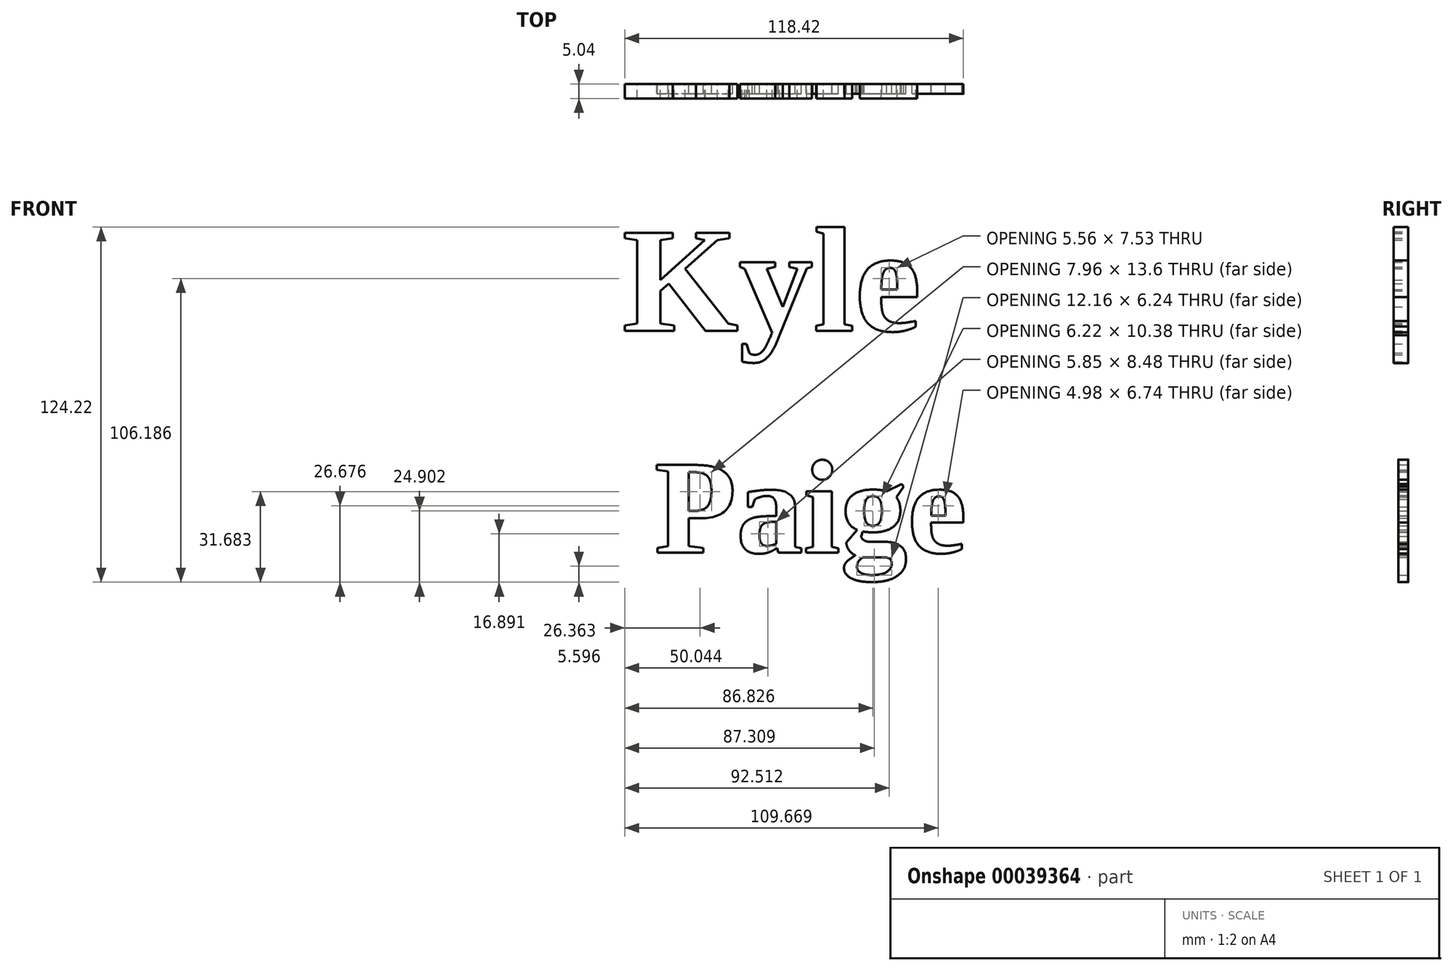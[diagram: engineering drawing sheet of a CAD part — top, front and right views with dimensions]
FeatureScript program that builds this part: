
annotation { "Feature Type Name" : "Feature", "Feature Type Description" : "" }
export const myFeature = defineFeature(function(context is Context, id is Id, definition is map)
    precondition{}
    {
        {
            var Q0;
            Q0=qCreatedBy(makeId("Front.planeOp"),FACE);
            var sketch = newSketch(context, id + "F0", { "sketchPlane" : qUnion([Q0])});
            skText(sketch, "E0", { "text": "Kyle", "fontName": "Tinos-Bold.ttf"});
            const initialGuessF0  = {"E0": [-0.05057, 0.01097, 1, 0, 0.03764]};
            skSetInitialGuess(sketch, initialGuessF0);
            skSolve(sketch);
        }
        {
            var Q0;
            Q0 = qSketchRegion(id + "F0", true);
            extrude(context, id + "F1", {"entities" : qUnion([Q0]), "depth" : 5.04 * mm});
        }
        {
            var Q0;
            Q0=makeQuery(id+"F1.opExtrude","SWEPT_BODY",BODY,{"disambiguationData":[OSD([sQuery(id+"F0.wireOp",EDGE,"E0.sketch_text.stroke-0"),sQuery(id+"F0.wireOp",EDGE,"E0.sketch_text.stroke-1"),sQuery(id+"F0.wireOp",EDGE,"E0.sketch_text.stroke-2"),sQuery(id+"F0.wireOp",EDGE,"E0.sketch_text.stroke-3"),sQuery(id+"F0.wireOp",EDGE,"E0.sketch_text.stroke-4"),sQuery(id+"F0.wireOp",EDGE,"E0.sketch_text.stroke-5"),sQuery(id+"F0.wireOp",EDGE,"E0.sketch_text.stroke-6"),sQuery(id+"F0.wireOp",EDGE,"E0.sketch_text.stroke-7"),sQuery(id+"F0.wireOp",EDGE,"E0.sketch_text.stroke-8"),sQuery(id+"F0.wireOp",EDGE,"E0.sketch_text.stroke-9"),sQuery(id+"F0.wireOp",EDGE,"E0.sketch_text.stroke-10"),sQuery(id+"F0.wireOp",EDGE,"E0.sketch_text.stroke-11"),sQuery(id+"F0.wireOp",EDGE,"E0.sketch_text.stroke-12"),sQuery(id+"F0.wireOp",EDGE,"E0.sketch_text.stroke-13"),sQuery(id+"F0.wireOp",EDGE,"E0.sketch_text.stroke-14"),sQuery(id+"F0.wireOp",EDGE,"E0.sketch_text.stroke-15"),sQuery(id+"F0.wireOp",EDGE,"E0.sketch_text.stroke-16"),sQuery(id+"F0.wireOp",EDGE,"E0.sketch_text.stroke-17"),sQuery(id+"F0.wireOp",EDGE,"E0.sketch_text.stroke-18"),sQuery(id+"F0.wireOp",EDGE,"E0.sketch_text.stroke-19"),sQuery(id+"F0.wireOp",EDGE,"E0.sketch_text.stroke-20"),sQuery(id+"F0.wireOp",EDGE,"E0.sketch_text.stroke-21"),sQuery(id+"F0.wireOp",EDGE,"E0.sketch_text.stroke-22"),sQuery(id+"F0.wireOp",EDGE,"E0.sketch_text.stroke-23"),sQuery(id+"F0.wireOp",EDGE,"E0.sketch_text.stroke-24"),sQuery(id+"F0.wireOp",EDGE,"E0.sketch_text.stroke-25")])]});
            var Q1;
            Q1=makeQuery(id+"F1.opExtrude","SWEPT_BODY",BODY,{"disambiguationData":[OSD([sQuery(id+"F0.wireOp",EDGE,"E0.sketch_text.stroke-26"),sQuery(id+"F0.wireOp",EDGE,"E0.sketch_text.stroke-27"),sQuery(id+"F0.wireOp",EDGE,"E0.sketch_text.stroke-28"),sQuery(id+"F0.wireOp",EDGE,"E0.sketch_text.stroke-29"),sQuery(id+"F0.wireOp",EDGE,"E0.sketch_text.stroke-30"),sQuery(id+"F0.wireOp",EDGE,"E0.sketch_text.stroke-31"),sQuery(id+"F0.wireOp",EDGE,"E0.sketch_text.stroke-32"),sQuery(id+"F0.wireOp",EDGE,"E0.sketch_text.stroke-33"),sQuery(id+"F0.wireOp",EDGE,"E0.sketch_text.stroke-34"),sQuery(id+"F0.wireOp",EDGE,"E0.sketch_text.stroke-35"),sQuery(id+"F0.wireOp",EDGE,"E0.sketch_text.stroke-36"),sQuery(id+"F0.wireOp",EDGE,"E0.sketch_text.stroke-37"),sQuery(id+"F0.wireOp",EDGE,"E0.sketch_text.stroke-38"),sQuery(id+"F0.wireOp",EDGE,"E0.sketch_text.stroke-39"),sQuery(id+"F0.wireOp",EDGE,"E0.sketch_text.stroke-40"),sQuery(id+"F0.wireOp",EDGE,"E0.sketch_text.stroke-41"),sQuery(id+"F0.wireOp",EDGE,"E0.sketch_text.stroke-42"),sQuery(id+"F0.wireOp",EDGE,"E0.sketch_text.stroke-43"),sQuery(id+"F0.wireOp",EDGE,"E0.sketch_text.stroke-44"),sQuery(id+"F0.wireOp",EDGE,"E0.sketch_text.stroke-45"),sQuery(id+"F0.wireOp",EDGE,"E0.sketch_text.stroke-46"),sQuery(id+"F0.wireOp",EDGE,"E0.sketch_text.stroke-47"),sQuery(id+"F0.wireOp",EDGE,"E0.sketch_text.stroke-48"),sQuery(id+"F0.wireOp",EDGE,"E0.sketch_text.stroke-49"),sQuery(id+"F0.wireOp",EDGE,"E0.sketch_text.stroke-50"),sQuery(id+"F0.wireOp",EDGE,"E0.sketch_text.stroke-51")])]});
            var Q2;
            Q2=makeQuery(id+"F1.opExtrude","SWEPT_BODY",BODY,{"disambiguationData":[OSD([sQuery(id+"F0.wireOp",EDGE,"E0.sketch_text.stroke-52"),sQuery(id+"F0.wireOp",EDGE,"E0.sketch_text.stroke-53"),sQuery(id+"F0.wireOp",EDGE,"E0.sketch_text.stroke-54"),sQuery(id+"F0.wireOp",EDGE,"E0.sketch_text.stroke-55"),sQuery(id+"F0.wireOp",EDGE,"E0.sketch_text.stroke-56"),sQuery(id+"F0.wireOp",EDGE,"E0.sketch_text.stroke-57"),sQuery(id+"F0.wireOp",EDGE,"E0.sketch_text.stroke-58"),sQuery(id+"F0.wireOp",EDGE,"E0.sketch_text.stroke-59"),sQuery(id+"F0.wireOp",EDGE,"E0.sketch_text.stroke-60"),sQuery(id+"F0.wireOp",EDGE,"E0.sketch_text.stroke-61")])]});
            var Q3;
            Q3=makeQuery(id+"F1.opExtrude","SWEPT_BODY",BODY,{"disambiguationData":[OSD([sQuery(id+"F0.wireOp",EDGE,"E0.sketch_text.stroke-62"),sQuery(id+"F0.wireOp",EDGE,"E0.sketch_text.stroke-63"),sQuery(id+"F0.wireOp",EDGE,"E0.sketch_text.stroke-64"),sQuery(id+"F0.wireOp",EDGE,"E0.sketch_text.stroke-65"),sQuery(id+"F0.wireOp",EDGE,"E0.sketch_text.stroke-66"),sQuery(id+"F0.wireOp",EDGE,"E0.sketch_text.stroke-67"),sQuery(id+"F0.wireOp",EDGE,"E0.sketch_text.stroke-68"),sQuery(id+"F0.wireOp",EDGE,"E0.sketch_text.stroke-69"),sQuery(id+"F0.wireOp",EDGE,"E0.sketch_text.stroke-70"),sQuery(id+"F0.wireOp",EDGE,"E0.sketch_text.stroke-71"),sQuery(id+"F0.wireOp",EDGE,"E0.sketch_text.stroke-72"),sQuery(id+"F0.wireOp",EDGE,"E0.sketch_text.stroke-73"),sQuery(id+"F0.wireOp",EDGE,"E0.sketch_text.stroke-74"),sQuery(id+"F0.wireOp",EDGE,"E0.sketch_text.stroke-75"),sQuery(id+"F0.wireOp",EDGE,"E0.sketch_text.stroke-76"),sQuery(id+"F0.wireOp",EDGE,"E0.sketch_text.stroke-77"),sQuery(id+"F0.wireOp",EDGE,"E0.sketch_text.stroke-78"),sQuery(id+"F0.wireOp",EDGE,"E0.sketch_text.stroke-79"),sQuery(id+"F0.wireOp",EDGE,"E0.sketch_text.stroke-80"),sQuery(id+"F0.wireOp",EDGE,"E0.sketch_text.stroke-81"),sQuery(id+"F0.wireOp",EDGE,"E0.sketch_text.stroke-82"),sQuery(id+"F0.wireOp",EDGE,"E0.sketch_text.stroke-83")])]});
            var Q4;
            Q4=makeQuery(id+"F1.opExtrude","CAP_VERTEX",VERTEX,{"disambiguationData":[OSD([sQuery(id+"F0.wireOp",EDGE,"E0.sketch_text.stroke-17"),sQuery(id+"F0.wireOp",EDGE,"E0.sketch_text.stroke-18")])],"isStart":false});
            transform(context, id + "F2", {"entities" : qUnion([Q0, Q1, Q2, Q3]), "transformType" : TransformType.SCALE_UNIFORMLY, "scale" : .5, "makeCopy" : false, "scalePoint" : qUnion([Q4])});
        }
        {
            var Q0;
            Q0=qCreatedBy(makeId("Front.planeOp"),FACE);
            var sketch = newSketch(context, id + "F3", { "sketchPlane" : qUnion([Q0])});
            skText(sketch, "E1", { "text": "Paige", "fontName": "Tinos-Bold.ttf"});
            const initialGuessF3  = {"E1": [-0.03925, -0.05045, 1, 0, 0.03371]};
            skSetInitialGuess(sketch, initialGuessF3);
            skSolve(sketch);
        }
        {
            var Q0;
            Q0=makeQuery(id+"F3.imprint","IMPRINT",FACE,{"disambiguationData":[TD([[makeQuery(id+"F3.imprint","IMPRINT",EDGE,{"derivedFrom":sQuery(id+"F3.wireOp",EDGE,"E1.sketch_text.stroke-0")}),-1.0]])]});
            var Q1;
            Q1=makeQuery(id+"F3.imprint","IMPRINT",FACE,{"disambiguationData":[TD([[makeQuery(id+"F3.imprint","IMPRINT",EDGE,{"derivedFrom":sQuery(id+"F3.wireOp",EDGE,"E1.sketch_text.stroke-21")}),-1.0]])]});
            var Q2;
            Q2=makeQuery(id+"F3.imprint","IMPRINT",FACE,{"disambiguationData":[TD([[makeQuery(id+"F3.imprint","IMPRINT",EDGE,{"derivedFrom":sQuery(id+"F3.wireOp",EDGE,"E1.sketch_text.stroke-49")}),-1.0]])]});
            var Q3;
            Q3=makeQuery(id+"F3.imprint","IMPRINT",FACE,{"disambiguationData":[TD([[makeQuery(id+"F3.imprint","IMPRINT",EDGE,{"derivedFrom":sQuery(id+"F3.wireOp",EDGE,"E1.sketch_text.stroke-67")}),-1.0]])]});
            var Q4;
            Q4=makeQuery(id+"F3.imprint","IMPRINT",FACE,{"disambiguationData":[TD([[makeQuery(id+"F3.imprint","IMPRINT",EDGE,{"derivedFrom":sQuery(id+"F3.wireOp",EDGE,"E1.sketch_text.stroke-109")}),-1.0]])]});
            var Q5;
            Q5=makeQuery(id+"F3.imprint","IMPRINT",FACE,{"disambiguationData":[TD([[makeQuery(id+"F3.imprint","IMPRINT",EDGE,{"derivedFrom":sQuery(id+"F3.wireOp",EDGE,"E1.sketch_text.stroke-59")}),-1.0]])]});
            extrude(context, id + "F4", {"entities" : qUnion([Q0, Q1, Q2, Q3, Q4, Q5]), "depth" : 3.48 * mm});
        }
        {
            var Q0;
            Q0=makeQuery(id+"F1.opExtrude","SWEPT_BODY",BODY,{"disambiguationData":[OSD([sQuery(id+"F0.wireOp",EDGE,"E0.sketch_text.stroke-0"),sQuery(id+"F0.wireOp",EDGE,"E0.sketch_text.stroke-1"),sQuery(id+"F0.wireOp",EDGE,"E0.sketch_text.stroke-2"),sQuery(id+"F0.wireOp",EDGE,"E0.sketch_text.stroke-3"),sQuery(id+"F0.wireOp",EDGE,"E0.sketch_text.stroke-4"),sQuery(id+"F0.wireOp",EDGE,"E0.sketch_text.stroke-5"),sQuery(id+"F0.wireOp",EDGE,"E0.sketch_text.stroke-6"),sQuery(id+"F0.wireOp",EDGE,"E0.sketch_text.stroke-7"),sQuery(id+"F0.wireOp",EDGE,"E0.sketch_text.stroke-8"),sQuery(id+"F0.wireOp",EDGE,"E0.sketch_text.stroke-9"),sQuery(id+"F0.wireOp",EDGE,"E0.sketch_text.stroke-10"),sQuery(id+"F0.wireOp",EDGE,"E0.sketch_text.stroke-11"),sQuery(id+"F0.wireOp",EDGE,"E0.sketch_text.stroke-12"),sQuery(id+"F0.wireOp",EDGE,"E0.sketch_text.stroke-13"),sQuery(id+"F0.wireOp",EDGE,"E0.sketch_text.stroke-14"),sQuery(id+"F0.wireOp",EDGE,"E0.sketch_text.stroke-15"),sQuery(id+"F0.wireOp",EDGE,"E0.sketch_text.stroke-16"),sQuery(id+"F0.wireOp",EDGE,"E0.sketch_text.stroke-17"),sQuery(id+"F0.wireOp",EDGE,"E0.sketch_text.stroke-18"),sQuery(id+"F0.wireOp",EDGE,"E0.sketch_text.stroke-19"),sQuery(id+"F0.wireOp",EDGE,"E0.sketch_text.stroke-20"),sQuery(id+"F0.wireOp",EDGE,"E0.sketch_text.stroke-21"),sQuery(id+"F0.wireOp",EDGE,"E0.sketch_text.stroke-22"),sQuery(id+"F0.wireOp",EDGE,"E0.sketch_text.stroke-23"),sQuery(id+"F0.wireOp",EDGE,"E0.sketch_text.stroke-24"),sQuery(id+"F0.wireOp",EDGE,"E0.sketch_text.stroke-25")])]});
            var Q1;
            Q1=makeQuery(id+"F1.opExtrude","SWEPT_BODY",BODY,{"disambiguationData":[OSD([sQuery(id+"F0.wireOp",EDGE,"E0.sketch_text.stroke-26"),sQuery(id+"F0.wireOp",EDGE,"E0.sketch_text.stroke-27"),sQuery(id+"F0.wireOp",EDGE,"E0.sketch_text.stroke-28"),sQuery(id+"F0.wireOp",EDGE,"E0.sketch_text.stroke-29"),sQuery(id+"F0.wireOp",EDGE,"E0.sketch_text.stroke-30"),sQuery(id+"F0.wireOp",EDGE,"E0.sketch_text.stroke-31"),sQuery(id+"F0.wireOp",EDGE,"E0.sketch_text.stroke-32"),sQuery(id+"F0.wireOp",EDGE,"E0.sketch_text.stroke-33"),sQuery(id+"F0.wireOp",EDGE,"E0.sketch_text.stroke-34"),sQuery(id+"F0.wireOp",EDGE,"E0.sketch_text.stroke-35"),sQuery(id+"F0.wireOp",EDGE,"E0.sketch_text.stroke-36"),sQuery(id+"F0.wireOp",EDGE,"E0.sketch_text.stroke-37"),sQuery(id+"F0.wireOp",EDGE,"E0.sketch_text.stroke-38"),sQuery(id+"F0.wireOp",EDGE,"E0.sketch_text.stroke-39"),sQuery(id+"F0.wireOp",EDGE,"E0.sketch_text.stroke-40"),sQuery(id+"F0.wireOp",EDGE,"E0.sketch_text.stroke-41"),sQuery(id+"F0.wireOp",EDGE,"E0.sketch_text.stroke-42"),sQuery(id+"F0.wireOp",EDGE,"E0.sketch_text.stroke-43"),sQuery(id+"F0.wireOp",EDGE,"E0.sketch_text.stroke-44"),sQuery(id+"F0.wireOp",EDGE,"E0.sketch_text.stroke-45"),sQuery(id+"F0.wireOp",EDGE,"E0.sketch_text.stroke-46"),sQuery(id+"F0.wireOp",EDGE,"E0.sketch_text.stroke-47"),sQuery(id+"F0.wireOp",EDGE,"E0.sketch_text.stroke-48"),sQuery(id+"F0.wireOp",EDGE,"E0.sketch_text.stroke-49"),sQuery(id+"F0.wireOp",EDGE,"E0.sketch_text.stroke-50"),sQuery(id+"F0.wireOp",EDGE,"E0.sketch_text.stroke-51")])]});
            var Q2;
            Q2=makeQuery(id+"F1.opExtrude","SWEPT_BODY",BODY,{"disambiguationData":[OSD([sQuery(id+"F0.wireOp",EDGE,"E0.sketch_text.stroke-52"),sQuery(id+"F0.wireOp",EDGE,"E0.sketch_text.stroke-53"),sQuery(id+"F0.wireOp",EDGE,"E0.sketch_text.stroke-54"),sQuery(id+"F0.wireOp",EDGE,"E0.sketch_text.stroke-55"),sQuery(id+"F0.wireOp",EDGE,"E0.sketch_text.stroke-56"),sQuery(id+"F0.wireOp",EDGE,"E0.sketch_text.stroke-57"),sQuery(id+"F0.wireOp",EDGE,"E0.sketch_text.stroke-58"),sQuery(id+"F0.wireOp",EDGE,"E0.sketch_text.stroke-59"),sQuery(id+"F0.wireOp",EDGE,"E0.sketch_text.stroke-60"),sQuery(id+"F0.wireOp",EDGE,"E0.sketch_text.stroke-61")])]});
            var Q3;
            Q3=makeQuery(id+"F1.opExtrude","SWEPT_BODY",BODY,{"disambiguationData":[OSD([sQuery(id+"F0.wireOp",EDGE,"E0.sketch_text.stroke-62"),sQuery(id+"F0.wireOp",EDGE,"E0.sketch_text.stroke-63"),sQuery(id+"F0.wireOp",EDGE,"E0.sketch_text.stroke-64"),sQuery(id+"F0.wireOp",EDGE,"E0.sketch_text.stroke-65"),sQuery(id+"F0.wireOp",EDGE,"E0.sketch_text.stroke-66"),sQuery(id+"F0.wireOp",EDGE,"E0.sketch_text.stroke-67"),sQuery(id+"F0.wireOp",EDGE,"E0.sketch_text.stroke-68"),sQuery(id+"F0.wireOp",EDGE,"E0.sketch_text.stroke-69"),sQuery(id+"F0.wireOp",EDGE,"E0.sketch_text.stroke-70"),sQuery(id+"F0.wireOp",EDGE,"E0.sketch_text.stroke-71"),sQuery(id+"F0.wireOp",EDGE,"E0.sketch_text.stroke-72"),sQuery(id+"F0.wireOp",EDGE,"E0.sketch_text.stroke-73"),sQuery(id+"F0.wireOp",EDGE,"E0.sketch_text.stroke-74"),sQuery(id+"F0.wireOp",EDGE,"E0.sketch_text.stroke-75"),sQuery(id+"F0.wireOp",EDGE,"E0.sketch_text.stroke-76"),sQuery(id+"F0.wireOp",EDGE,"E0.sketch_text.stroke-77"),sQuery(id+"F0.wireOp",EDGE,"E0.sketch_text.stroke-78"),sQuery(id+"F0.wireOp",EDGE,"E0.sketch_text.stroke-79"),sQuery(id+"F0.wireOp",EDGE,"E0.sketch_text.stroke-80"),sQuery(id+"F0.wireOp",EDGE,"E0.sketch_text.stroke-81"),sQuery(id+"F0.wireOp",EDGE,"E0.sketch_text.stroke-82"),sQuery(id+"F0.wireOp",EDGE,"E0.sketch_text.stroke-83")])]});
            var Q4;
            Q4=makeQuery(id+"F1.opExtrude","CAP_VERTEX",VERTEX,{"disambiguationData":[OSD([sQuery(id+"F0.wireOp",EDGE,"E0.sketch_text.stroke-13"),sQuery(id+"F0.wireOp",EDGE,"E0.sketch_text.stroke-14")])],"isStart":false});
            transform(context, id + "F5", {"entities" : qUnion([Q0, Q1, Q2, Q3]), "transformType" : TransformType.SCALE_UNIFORMLY, "scale" : 2, "makeCopy" : false, "scalePoint" : qUnion([Q4])});
        }
    });
